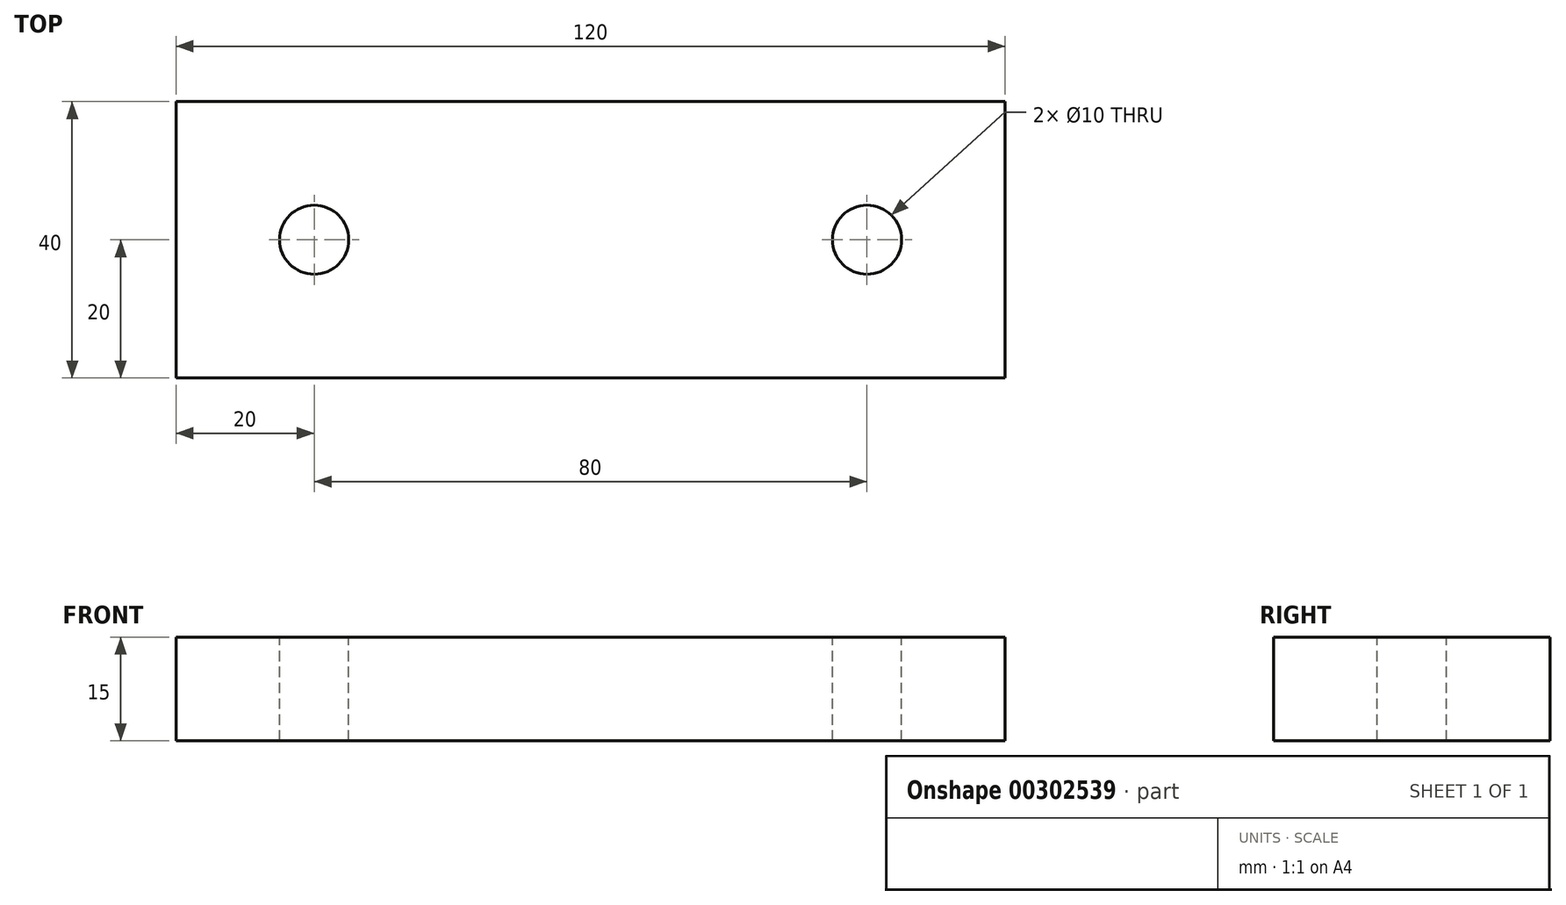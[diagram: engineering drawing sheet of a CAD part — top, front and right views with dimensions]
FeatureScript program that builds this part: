
annotation { "Feature Type Name" : "Feature", "Feature Type Description" : "" }
export const myFeature = defineFeature(function(context is Context, id is Id, definition is map)
    precondition{}
    {
        {
            var Q0;
            Q0=qCreatedBy(makeId("Top.planeOp"),FACE);
            var sketch = newSketch(context, id + "F0", { "sketchPlane" : qUnion([Q0])});
            skLineSegment(sketch, "E0.bottom", {"start": v(0, 0) * mm, "end": v(120, 0) * mm});
            skLineSegment(sketch, "E0.top", {"start": v(0, 40) * mm, "end": v(120, 40) * mm});
            skLineSegment(sketch, "E0.left", {"start": v(0, 0) * mm, "end": v(0, 40) * mm});
            skLineSegment(sketch, "E0.right", {"start": v(120, 0) * mm, "end": v(120, 40) * mm});
            skCircle(sketch, "E1", {"center": v(20, 20) * mm, "radius": 5 * mm});
            skCircle(sketch, "E2", {"center": v(100, 20) * mm, "radius": 5 * mm});
            skSolve(sketch);
        }
        {
            var Q0;
            Q0=makeQuery(id+"F0.imprint","IMPRINT",FACE,{"disambiguationData":[TD([[makeQuery(id+"F0.imprint","IMPRINT",EDGE,{"derivedFrom":sQuery(id+"F0.wireOp",EDGE,"E0.bottom")}),1.0]])]});
            extrude(context, id + "F1", {"entities" : qUnion([Q0]), "oppositeDirection" : true, "depth" : 15 * mm});
        }
    });
